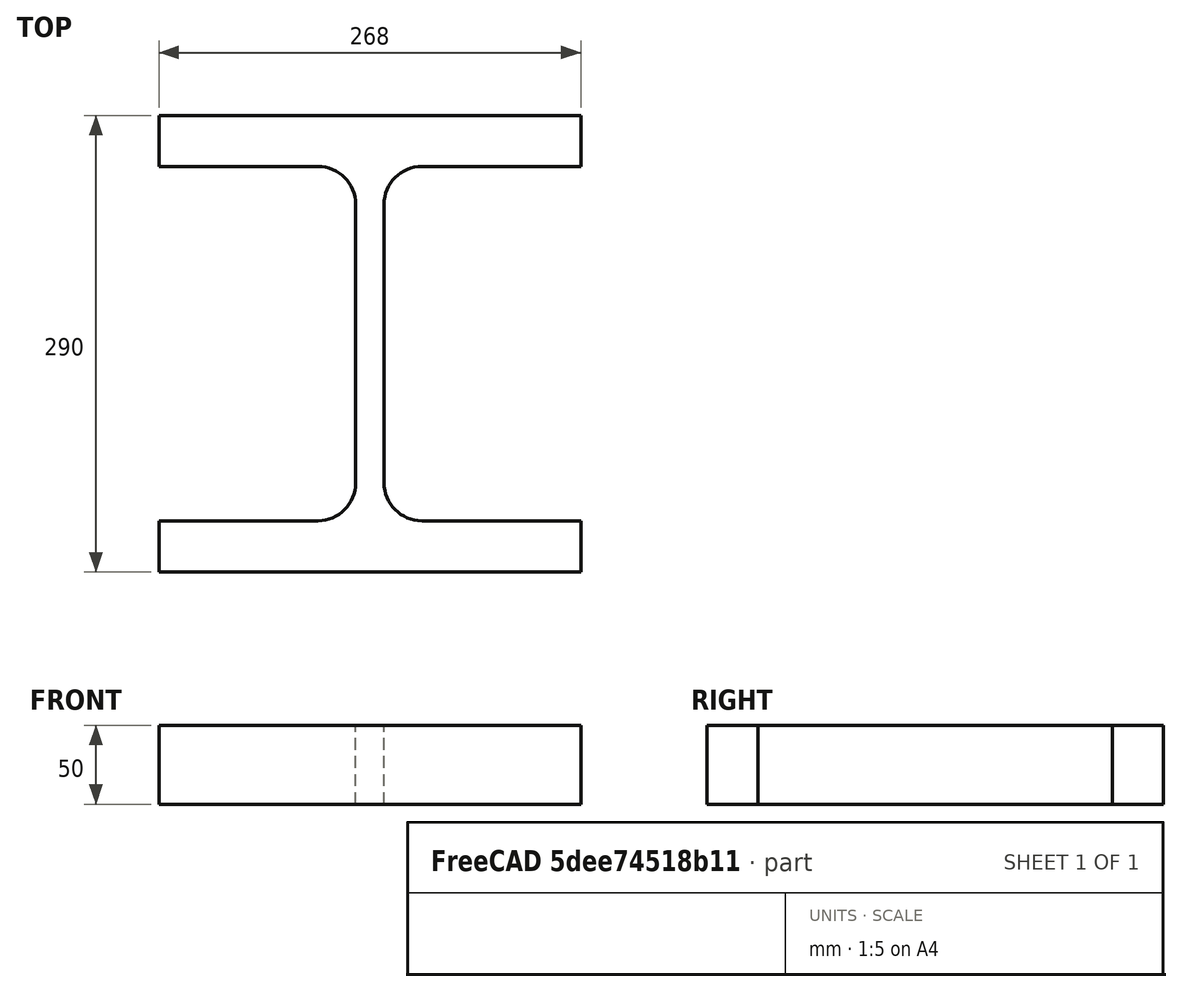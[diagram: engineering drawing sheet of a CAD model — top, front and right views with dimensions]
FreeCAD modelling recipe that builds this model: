
FCSTD DOCUMENT  (FreeCAD 0.15R4671 (Git))
Label: HE-M-Profile 260 DIN1025-4 S235JR
License: All rights reserved
LicenseURL: http://en.wikipedia.org/wiki/All_rights_reserved
objects: Sketcher::SketchObject×1, Part::Extrusion×1
note: 2 computed .brp shape members not serialized (recipe doc carries the construction recipe); baked Part::Feature solids carry a one-line shape summary decoded from their .brp

FEATURE [Sketcher::SketchObject] Sketch
  sketch-geometry (16):
    g0: LineSegment StartX=9 StartY=-88.5 StartZ=0 EndX=9 EndY=88.5 EndZ=0
    g1: LineSegment StartX=33 StartY=112.5 StartZ=0 EndX=134 EndY=112.5 EndZ=0
    g2: LineSegment StartX=134 StartY=112.5 StartZ=0 EndX=134 EndY=145 EndZ=0
    g3: LineSegment StartX=134 StartY=145 StartZ=0 EndX=-134 EndY=145 EndZ=0
    g4: LineSegment StartX=-134 StartY=145 StartZ=0 EndX=-134 EndY=112.5 EndZ=0
    g5: LineSegment StartX=-134 StartY=112.5 StartZ=0 EndX=-33 EndY=112.5 EndZ=0
    g6: LineSegment StartX=-9 StartY=88.5 StartZ=0 EndX=-9 EndY=-88.5 EndZ=0
    g7: LineSegment StartX=-33 StartY=-112.5 StartZ=0 EndX=-134 EndY=-112.5 EndZ=0
    g8: LineSegment StartX=-134 StartY=-112.5 StartZ=0 EndX=-134 EndY=-145 EndZ=0
    g9: LineSegment StartX=-134 StartY=-145 StartZ=0 EndX=134 EndY=-145 EndZ=0
    g10: LineSegment StartX=134 StartY=-145 StartZ=0 EndX=134 EndY=-112.5 EndZ=0
    g11: LineSegment StartX=134 StartY=-112.5 StartZ=0 EndX=33 EndY=-112.5 EndZ=0
    g12: ArcOfCircle CenterX=33 CenterY=88.5 CenterZ=0 NormalX=0 NormalY=0 NormalZ=1 Radius=24 StartAngle=1.5708 EndAngle=3.14159
    g13: ArcOfCircle CenterX=33 CenterY=-88.5 CenterZ=0 NormalX=0 NormalY=0 NormalZ=1 Radius=24 StartAngle=3.14159 EndAngle=4.71239
    g14: ArcOfCircle CenterX=-33 CenterY=88.5 CenterZ=0 NormalX=0 NormalY=0 NormalZ=1 Radius=24 StartAngle=0 EndAngle=1.5708
    g15: ArcOfCircle CenterX=-33 CenterY=-88.5 CenterZ=0 NormalX=0 NormalY=0 NormalZ=1 Radius=24 StartAngle=4.71239 EndAngle=6.28319
  constraints (42):
    c: Vertical(g0)
    c: Coincident(g2,g1)
    c: Vertical(g2)
    c: Coincident(g3,g2)
    c: Coincident(g4,g3)
    c: Vertical(g4)
    c: Coincident(g5,g4)
    c: Horizontal(g5)
    c: Vertical(g6)
    c: Horizontal(g7)
    c: Coincident(g8,g7)
    c: Vertical(g8)
    c: Coincident(g9,g8)
    c: Horizontal(g9)
    c: Coincident(g10,g9)
    c: Vertical(g10)
    c: Coincident(g11,g10)
    c: Horizontal(g11)
    c: Tangent(g1,g12) = 1.5708
    c: Tangent(g0,g12) = 1.5708
    c: Tangent(g0,g13) = 1.5708
    c: Tangent(g11,g13) = 1.5708
    c: Tangent(g5,g14) = 1.5708
    c: Tangent(g6,g14) = 1.5708
    c: Tangent(g6,g15) = 1.5708
    c: Tangent(g7,g15) = 1.5708
    c: Equal(g3,g9)
    c: Equal(g2,g4)
    c: Equal(g4,g8)
    c: Equal(g8,g10)
    c: Equal(g12,g14)
    c: Equal(g14,g15)
    c: Equal(g15,g13)
    c: Symmetric(g2,g3,g-2)
    c: Symmetric(g9,g8,g-2)
    c: Symmetric(g0,g6,g-2)
    c: Symmetric(g2,g9,g-1)
    c: DistanceY(g2,g9) = -290
    c: DistanceX(g3) = -268
    c: DistanceX(g0,g6) = -18
    c: DistanceY(g2) = 32.5
    c: Radius(g12) = 24
FEATURE [Part::Extrusion] Extrude  label="HE-M-Profile 260 DIN1025-4 S235JR"
  Base = -> Sketch
  Dir = (0,0,50)
  Solid = true
